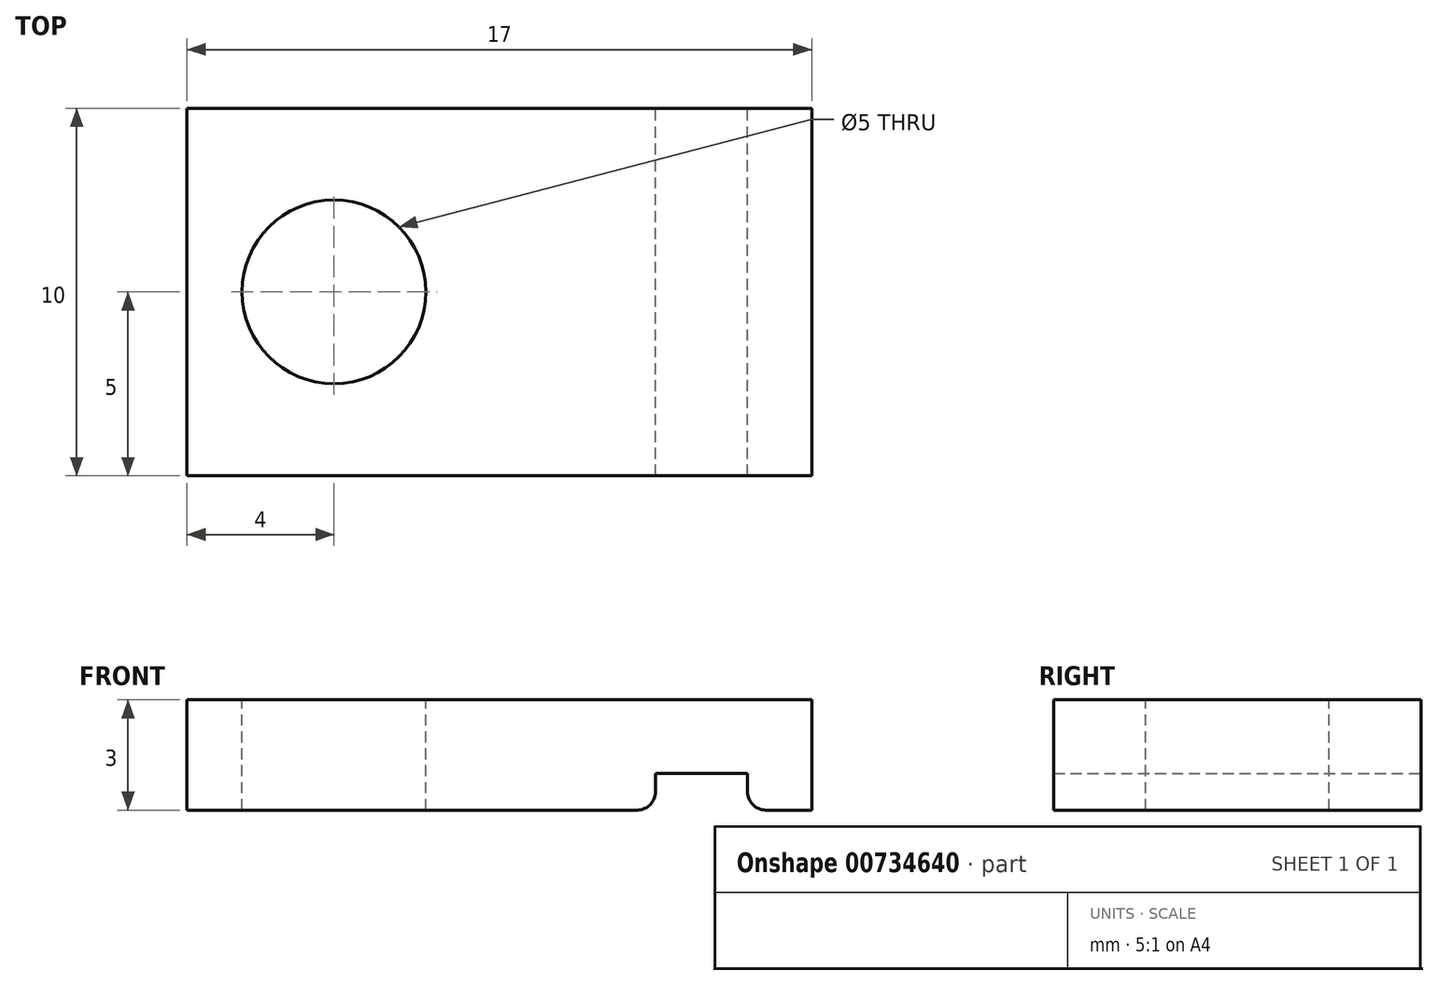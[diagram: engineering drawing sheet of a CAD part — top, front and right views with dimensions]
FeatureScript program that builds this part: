
annotation { "Feature Type Name" : "Feature", "Feature Type Description" : "" }
export const myFeature = defineFeature(function(context is Context, id is Id, definition is map)
    precondition{}
    {
        {
            var Q0;
            Q0=qCreatedBy(makeId("Front.planeOp"),FACE);
            var sketch = newSketch(context, id + "F0", { "sketchPlane" : qUnion([Q0])});
            skLineSegment(sketch, "E0.bottom", {"start": v(0, 0) * mm, "end": v(12.75, 0) * mm});
            skLineSegment(sketch, "E0.top", {"start": v(0, 3) * mm, "end": v(17, 3) * mm});
            skLineSegment(sketch, "E0.left", {"start": v(0, 0) * mm, "end": v(0, 3) * mm});
            skLineSegment(sketch, "E0.right", {"start": v(17, 0) * mm, "end": v(17, 3) * mm});
            skLineSegment(sketch, "E1.top", {"start": v(15.25, 1) * mm, "end": v(12.75, 1) * mm});
            skLineSegment(sketch, "E1.left", {"start": v(15.25, 0) * mm, "end": v(15.25, 1) * mm});
            skLineSegment(sketch, "E1.right", {"start": v(12.75, 0) * mm, "end": v(12.75, 1) * mm});
            skLineSegment(sketch, "E2.trimOffspring", {"start": v(15.25, 0) * mm, "end": v(17, 0) * mm});
            skSolve(sketch);
        }
        {
            var Q0;
            Q0 = qSketchRegion(id + "F0", true);
            extrude(context, id + "F1", {"entities" : qUnion([Q0]), "depth" : 5 * mm, "offsetDistance" : 25 * mm, "hasSecondDirection" : true, "secondDirectionOppositeDirection" : true, "secondDirectionDepth" : 5 * mm});
        }
        {
            var Q0;
            Q0=makeQuery(id+"F1.opExtrude","SWEPT_FACE",FACE,{"disambiguationData":[OSD([sQuery(id+"F0.wireOp",EDGE,"E0.top")])]});
            var sketch = newSketch(context, id + "F2", { "sketchPlane" : qUnion([Q0])});
            skCircle(sketch, "E3", {"center": v(4, 0) * mm, "radius": 2.5 * mm});
            skSolve(sketch);
        }
        {
            var Q0;
            Q0 = qSketchRegion(id + "F2", true);
            extrude(context, id + "F3", {"entities" : qUnion([Q0]), "operationType" : NewBodyOperationType.REMOVE, "endBound" : BoundingType.THROUGH_ALL, "oppositeDirection" : true, "depth" : 25 * mm, "offsetDistance" : 25 * mm});
        }
        {
            var Q0;
            Q0=makeQuery(id+"F1.opExtrude","SWEPT_EDGE",EDGE,{"disambiguationData":[OSD([sQuery(id+"F0.wireOp",EDGE,"E0.bottom"),sQuery(id+"F0.wireOp",EDGE,"E1.right")])]});
            var Q1;
            Q1=makeQuery(id+"F1.opExtrude","SWEPT_EDGE",EDGE,{"disambiguationData":[OSD([sQuery(id+"F0.wireOp",EDGE,"E1.left"),sQuery(id+"F0.wireOp",EDGE,"E2.trimOffspring")])]});
            fillet(context, id + "F4", {"entities" : qUnion([Q0, Q1]), "tangentPropagation" : true, "radius" : 0.5 * mm, "defaultsChanged" : false, "vertexSettings" : [], "allowEdgeOverflow" : false});
        }
    });
